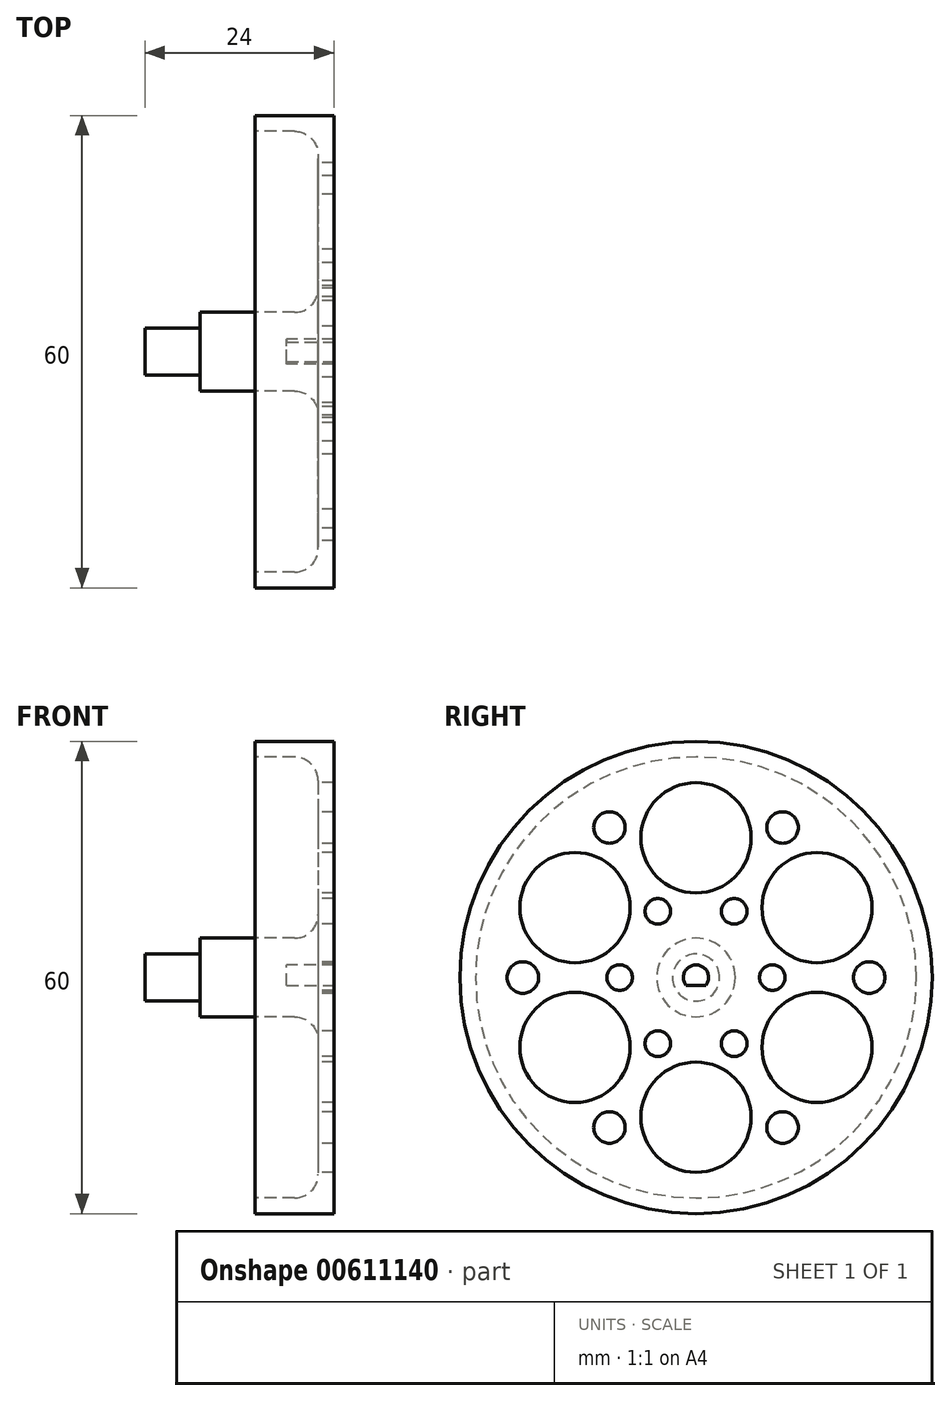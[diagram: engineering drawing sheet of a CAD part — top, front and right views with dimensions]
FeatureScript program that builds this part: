
annotation { "Feature Type Name" : "Feature", "Feature Type Description" : "" }
export const myFeature = defineFeature(function(context is Context, id is Id, definition is map)
    precondition{}
    {
        {
            var Q0;
            Q0=qCreatedBy(makeId("Front.planeOp"),FACE);
            var sketch = newSketch(context, id + "F0", { "sketchPlane" : qUnion([Q0])});
            skLineSegment(sketch, "E0", {"start": v(-67.26, 0) * mm, "end": v(-6, 0) * mm, "construction": true});
            skLineSegment(sketch, "E1.bottom", {"start": v(-2, 0) * mm, "end": v(0, 0) * mm});
            skLineSegment(sketch, "E1.left", {"start": v(-2, 8) * mm, "end": v(-2, 25) * mm});
            skLineSegment(sketch, "E2.bottom", {"start": v(-5, 28) * mm, "end": v(-10, 28) * mm});
            skLineSegment(sketch, "E2.top", {"start": v(0, 30) * mm, "end": v(-10, 30) * mm});
            skLineSegment(sketch, "E2.left", {"start": v(0, 28) * mm, "end": v(0, 30) * mm});
            skLineSegment(sketch, "E2.right", {"start": v(-10, 28) * mm, "end": v(-10, 30) * mm});
            skArc(sketch, "E3.filletArc", {"start": v(-2, 25) * mm, "mid": v(-2.88, 27.12) * mm, "end": v(-5, 28) * mm});
            skLineSegment(sketch, "E4.bottom", {"start": v(-6, 0) * mm, "end": v(-17, 0) * mm});
            skLineSegment(sketch, "E4.top", {"start": v(-5, 5) * mm, "end": v(-17, 5) * mm});
            skLineSegment(sketch, "E4.right", {"start": v(-17, 3) * mm, "end": v(-17, 5) * mm});
            skLineSegment(sketch, "E5.bottom", {"start": v(-24, 3) * mm, "end": v(-17, 3) * mm});
            skLineSegment(sketch, "E5.top", {"start": v(-24, 0) * mm, "end": v(-17, 0) * mm});
            skLineSegment(sketch, "E5.left", {"start": v(-24, 3) * mm, "end": v(-24, 0) * mm});
            skLineSegment(sketch, "E6.bottom", {"start": v(-6, 1.6) * mm, "end": v(0, 1.6) * mm});
            skLineSegment(sketch, "E6.left", {"start": v(-6, 1.6) * mm, "end": v(-6, 0) * mm});
            skLineSegment(sketch, "E7.trimOffspring", {"start": v(0, 0) * mm, "end": v(63.26, 0) * mm, "construction": true});
            skPoint(sketch, "E8.visualSharp", {"position": v(-2, 5) * mm});
            skArc(sketch, "E8.filletArc", {"start": v(-5, 5) * mm, "mid": v(-2.88, 5.88) * mm, "end": v(-2, 8) * mm});
            skLineSegment(sketch, "E9", {"start": v(0, 1.6) * mm, "end": v(0, 30) * mm});
            skSolve(sketch);
        }
        {
            var Q0;
            Q0=makeQuery(id+"F0.imprint","IMPRINT",FACE,{"disambiguationData":[TD([[makeQuery(id+"F0.imprint","IMPRINT",EDGE,{"derivedFrom":sQuery(id+"F0.wireOp",EDGE,"E1.left")}),-1.0]])]});
            var Q1;
            Q1=sQuery(id+"F0.wireOp",EDGE,"E0");
            revolve(context, id + "F1", {"entities" : qUnion([Q0]), "axis" : qUnion([Q1]), "revolveType" : RevolveType.FULL});
        }
        {
            var Q0;
            Q0=makeQuery(id+"F1.opRevolve","SWEPT_FACE",FACE,{"disambiguationData":[OSD([sQuery(id+"F0.wireOp",EDGE,"E9")])]});
            var sketch = newSketch(context, id + "F2", { "sketchPlane" : qUnion([Q0])});
            skLineSegment(sketch, "E10", {"start": v(-1.25, -1) * mm, "end": v(1.25, -1) * mm});
            skSolve(sketch);
        }
        {
            var Q0;
            Q0 = qSketchRegion(id + "F2", true);
            var Q1;
            {var subQ0=sQuery(id+"F2.wireOp",EDGE,"E10");Q1=makeQuery(id+"F2.imprint","IMPRINT",FACE,{"disambiguationData":[TD([[makeQuery(id+"F2.imprint","IMPRINT",EDGE,{"derivedFrom":subQ0}),-1.0]])]});}
            extrude(context, id + "F3", {"entities" : qUnion([Q0, Q1]), "operationType" : NewBodyOperationType.ADD, "oppositeDirection" : true, "depth" : 6 * mm, "offsetDistance" : 25 * mm});
        }
        {
            var Q0;
            Q0=makeQuery(id+"F1.opRevolve","SWEPT_FACE",FACE,{"disambiguationData":[OSD([sQuery(id+"F0.wireOp",EDGE,"E1.left")])]});
            var sketch = newSketch(context, id + "F4", { "sketchPlane" : qUnion([Q0])});
            skLineSegment(sketch, "E11", {"start": v(0, 0) * mm, "end": v(0, 30.23) * mm, "construction": true});
            skLineSegment(sketch, "E12", {"start": v(0, 0) * mm, "end": v(-30.35, 0) * mm, "construction": true});
            skSolve(sketch);
        }
        {
            var Q0;
            {var subQ0=sQuery(id+"F0.wireOp",EDGE,"E1.left");Q0=makeQuery(id+"F4.imprint","IMPRINT",FACE,{"disambiguationData":[TD([[makeQuery(id+"F4.imprint","IMPRINT",EDGE,{"derivedFrom":makeQuery(id+"F1.opRevolve","SWEPT_EDGE",EDGE,{"disambiguationData":[OSD([subQ0,sQuery(id+"F0.wireOp",EDGE,"E8.filletArc")])]})}),-1.0]])]});}
            var sketch = newSketch(context, id + "F5", { "sketchPlane" : qUnion([Q0])});
            skLineSegment(sketch, "E13", {"start": v(0, 0) * mm, "end": v(0, 35.5) * mm, "construction": true});
            skLineSegment(sketch, "E14", {"start": v(-35.63, 0) * mm, "end": v(35.65, 0) * mm, "construction": true});
            skCircle(sketch, "E15", {"center": v(0, 17.75) * mm, "radius": 7 * mm});
            skCircle(sketch, "E16.1.0", {"center": v(-15.37, 8.88) * mm, "radius": 7 * mm});
            skCircle(sketch, "E16.2.0", {"center": v(-15.37, -8.87) * mm, "radius": 7 * mm});
            skCircle(sketch, "E16.3.0", {"center": v(0, -17.75) * mm, "radius": 7 * mm});
            skCircle(sketch, "E16.4.0", {"center": v(15.37, -8.88) * mm, "radius": 7 * mm});
            skCircle(sketch, "E16.5.0", {"center": v(15.37, 8.88) * mm, "radius": 7 * mm});
            skPoint(sketch, "E16.center", {"position": v(0, 0) * mm});
            skLineSegment(sketch, "E17", {"start": v(0, 0) * mm, "end": v(-26.57, 15.43) * mm, "construction": true});
            skLineSegment(sketch, "E18", {"start": v(-15.37, 8.88) * mm, "end": v(0, 17.75) * mm, "construction": true});
            skLineSegment(sketch, "E19", {"start": v(0, 0) * mm, "end": v(-7.69, 13.31) * mm, "construction": true});
            skLineSegment(sketch, "E20", {"start": v(-7.69, 13.31) * mm, "end": v(-14.9, 25.8) * mm, "construction": true});
            skCircle(sketch, "E21", {"center": v(-11, 19.05) * mm, "radius": 2 * mm});
            skCircle(sketch, "E22", {"center": v(-4.85, 8.4) * mm, "radius": 1.63 * mm});
            skCircle(sketch, "E23.1.0", {"center": v(-22, 0) * mm, "radius": 2 * mm});
            skCircle(sketch, "E23.1.1", {"center": v(-9.7, 0) * mm, "radius": 1.63 * mm});
            skCircle(sketch, "E23.2.0", {"center": v(-11, -19.05) * mm, "radius": 2 * mm});
            skCircle(sketch, "E23.2.1", {"center": v(-4.85, -8.4) * mm, "radius": 1.63 * mm});
            skCircle(sketch, "E23.3.0", {"center": v(11, -19.05) * mm, "radius": 2 * mm});
            skCircle(sketch, "E23.3.1", {"center": v(4.85, -8.4) * mm, "radius": 1.63 * mm});
            skCircle(sketch, "E23.4.0", {"center": v(22, 0) * mm, "radius": 2 * mm});
            skCircle(sketch, "E23.4.1", {"center": v(9.7, 0) * mm, "radius": 1.63 * mm});
            skCircle(sketch, "E23.5.0", {"center": v(11, 19.05) * mm, "radius": 2 * mm});
            skCircle(sketch, "E23.5.1", {"center": v(4.85, 8.4) * mm, "radius": 1.63 * mm});
            skSolve(sketch);
        }
        {
            var Q0;
            Q0 = qSketchRegion(id + "F5", true);
            extrude(context, id + "F6", {"entities" : qUnion([Q0]), "operationType" : NewBodyOperationType.REMOVE, "oppositeDirection" : true, "depth" : 2 * mm, "offsetDistance" : 25 * mm});
        }
    });
